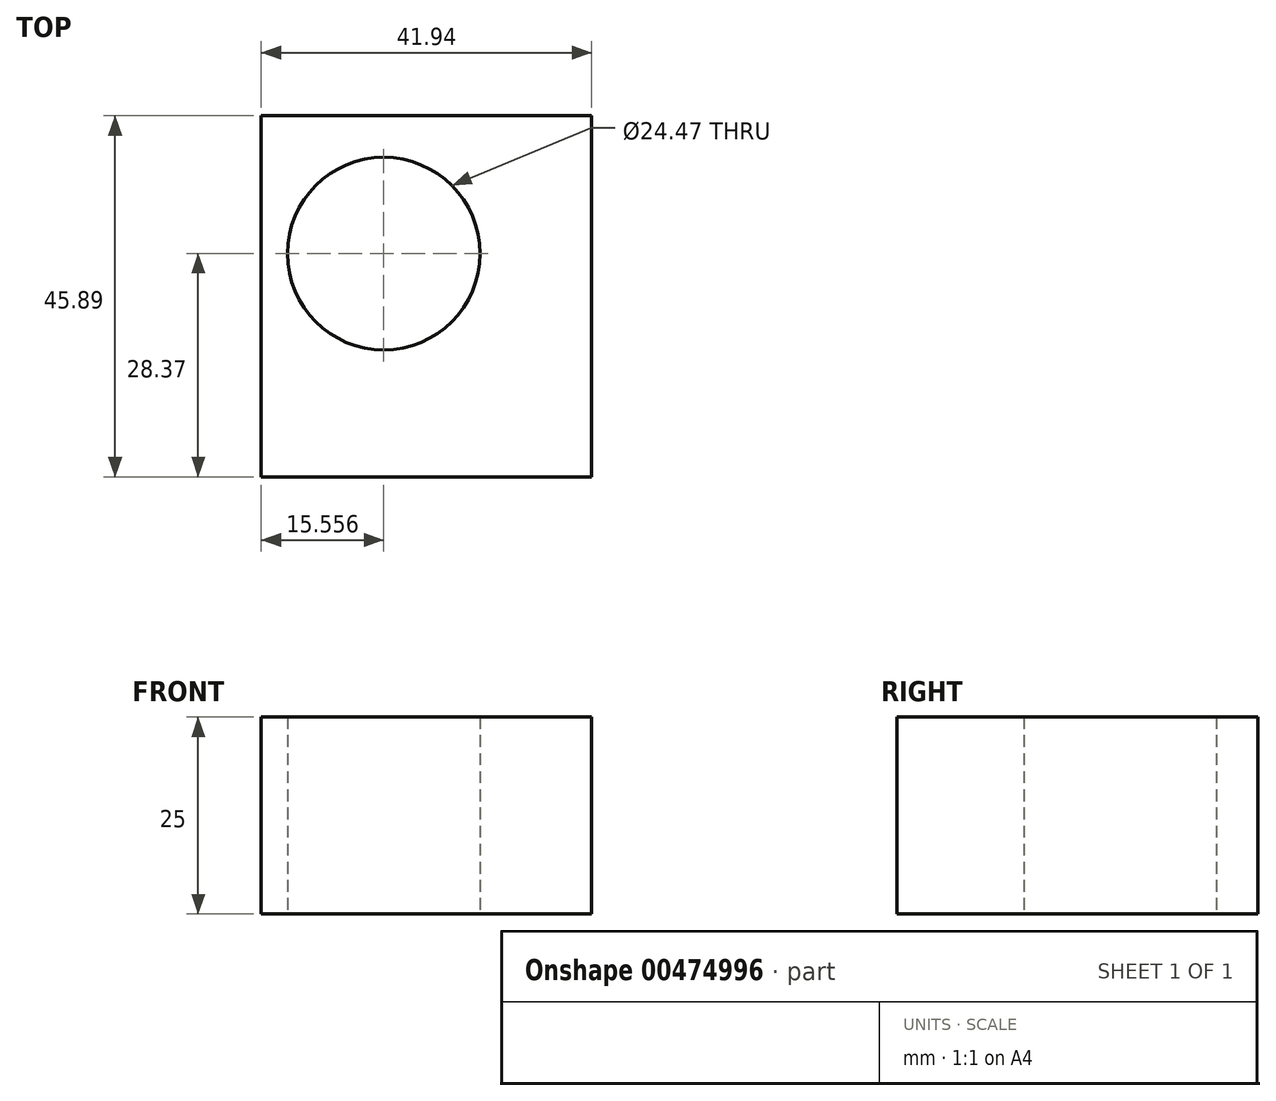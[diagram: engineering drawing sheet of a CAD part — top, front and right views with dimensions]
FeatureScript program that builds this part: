
annotation { "Feature Type Name" : "Feature", "Feature Type Description" : "" }
export const myFeature = defineFeature(function(context is Context, id is Id, definition is map)
    precondition{}
    {
        {
            var Q0;
            Q0=qCreatedBy(makeId("Top.planeOp"),FACE);
            var sketch = newSketch(context, id + "F0", { "sketchPlane" : qUnion([Q0])});
            skLineSegment(sketch, "E0.bottom", {"start": v(0, 0) * mm, "end": v(41.94, 0) * mm});
            skLineSegment(sketch, "E0.top", {"start": v(0, 45.89) * mm, "end": v(41.94, 45.89) * mm});
            skLineSegment(sketch, "E0.left", {"start": v(0, 0) * mm, "end": v(0, 45.89) * mm});
            skLineSegment(sketch, "E0.right", {"start": v(41.94, 0) * mm, "end": v(41.94, 45.89) * mm});
            skCircle(sketch, "E1", {"center": v(15.56, 28.37) * mm, "radius": 12.24 * mm});
            skSolve(sketch);
        }
        {
            var Q0;
            Q0 = qSketchRegion(id + "F0", true);
            extrude(context, id + "F1", {"entities" : qUnion([Q0]), "depth" : 25 * mm});
        }
    });
